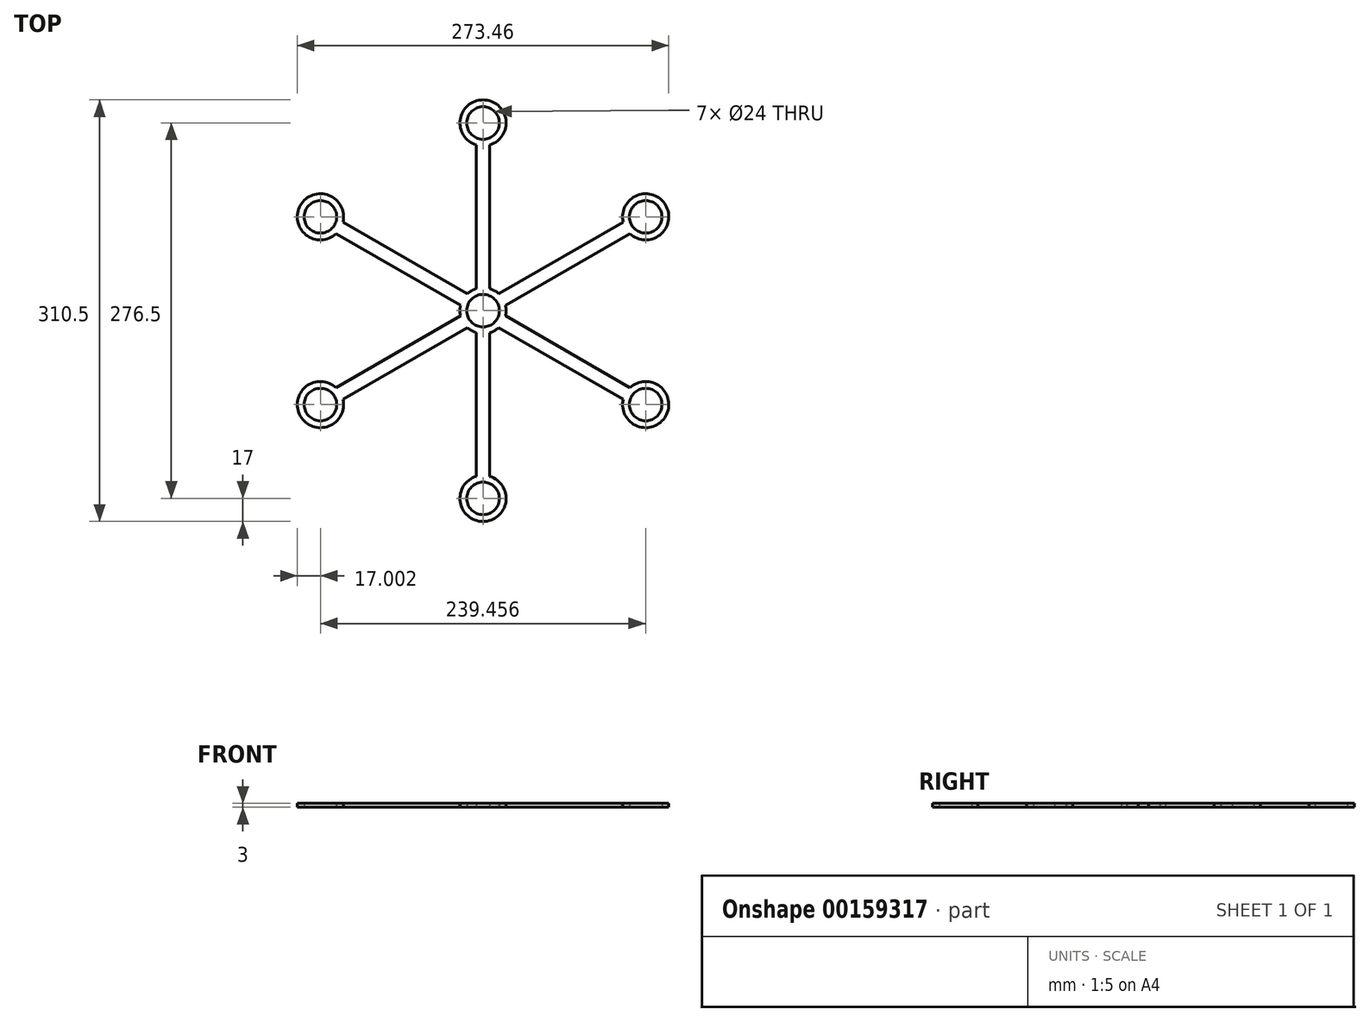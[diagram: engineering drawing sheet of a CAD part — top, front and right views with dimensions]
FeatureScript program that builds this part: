
annotation { "Feature Type Name" : "Feature", "Feature Type Description" : "" }
export const myFeature = defineFeature(function(context is Context, id is Id, definition is map)
    precondition{}
    {
        {
            var Q0;
            Q0=qCreatedBy(makeId("Top.planeOp"),FACE);
            var sketch = newSketch(context, id + "F0", { "sketchPlane" : qUnion([Q0])});
            skLineSegment(sketch, "E0", {"start": v(0, 0) * mm, "end": v(0, 138.25) * mm, "construction": true});
            skCircle(sketch, "E1", {"center": v(0, 0) * mm, "radius": 12 * mm});
            skCircle(sketch, "E2", {"center": v(0, 138.25) * mm, "radius": 12 * mm});
            skArc(sketch, "E3", {"start": v(5, 122) * mm, "mid": v(0, 155.25) * mm, "end": v(-5, 122) * mm});
            skArc(sketch, "E4", {"start": v(-16.57, 3.8) * mm, "mid": v(-17, 0) * mm, "end": v(-16.57, -3.8) * mm});
            skLineSegment(sketch, "E5", {"start": v(-5, 122) * mm, "end": v(-5, 16.25) * mm});
            skLineSegment(sketch, "E6", {"start": v(5, 122) * mm, "end": v(5, 16.25) * mm});
            skLineSegment(sketch, "E7.1.1", {"start": v(-108.16, 56.67) * mm, "end": v(-16.57, 3.8) * mm});
            skArc(sketch, "E7.1.2", {"start": v(-103.16, 65.33) * mm, "mid": v(-134.45, 77.63) * mm, "end": v(-108.16, 56.67) * mm});
            skLineSegment(sketch, "E7.1.3", {"start": v(-103.16, 65.33) * mm, "end": v(-11.57, 12.45) * mm});
            skCircle(sketch, "E7.1.4", {"center": v(-119.73, 69.13) * mm, "radius": 12 * mm});
            skLineSegment(sketch, "E7.1.6", {"start": v(0, 0) * mm, "end": v(-119.73, 69.13) * mm, "construction": true});
            skArc(sketch, "E7.2.0", {"start": v(-5, 16.25) * mm, "mid": v(-8.5, 14.72) * mm, "end": v(-11.57, 12.45) * mm});
            skLineSegment(sketch, "E7.2.1", {"start": v(-103.16, -65.33) * mm, "end": v(-11.57, -12.45) * mm});
            skArc(sketch, "E7.2.2", {"start": v(-108.16, -56.67) * mm, "mid": v(-134.45, -77.62) * mm, "end": v(-103.16, -65.33) * mm});
            skLineSegment(sketch, "E7.2.3", {"start": v(-108.16, -56.67) * mm, "end": v(-16.57, -3.8) * mm});
            skCircle(sketch, "E7.2.4", {"center": v(-119.73, -69.12) * mm, "radius": 12 * mm});
            skLineSegment(sketch, "E7.2.6", {"start": v(0, 0) * mm, "end": v(-119.73, -69.13) * mm, "construction": true});
            skArc(sketch, "E7.3.0", {"start": v(-5, 16.25) * mm, "mid": v(-8.5, 14.72) * mm, "end": v(-11.57, 12.45) * mm});
            skLineSegment(sketch, "E7.3.1", {"start": v(5, -122) * mm, "end": v(5, -16.25) * mm});
            skArc(sketch, "E7.3.2", {"start": v(-5, -122) * mm, "mid": v(0, -155.25) * mm, "end": v(5, -122) * mm});
            skLineSegment(sketch, "E7.3.3", {"start": v(-5, -122) * mm, "end": v(-5, -16.25) * mm});
            skCircle(sketch, "E7.3.4", {"center": v(0, -138.25) * mm, "radius": 12 * mm});
            skLineSegment(sketch, "E7.3.6", {"start": v(0, 0) * mm, "end": v(0, -138.25) * mm, "construction": true});
            skLineSegment(sketch, "E7.4.1", {"start": v(108.16, -56.67) * mm, "end": v(16.57, -3.8) * mm});
            skArc(sketch, "E7.4.2", {"start": v(103.16, -65.33) * mm, "mid": v(134.45, -77.63) * mm, "end": v(108.16, -56.67) * mm});
            skLineSegment(sketch, "E7.4.3", {"start": v(103.16, -65.33) * mm, "end": v(11.57, -12.45) * mm});
            skCircle(sketch, "E7.4.4", {"center": v(119.73, -69.13) * mm, "radius": 12 * mm});
            skLineSegment(sketch, "E7.4.6", {"start": v(0, 0) * mm, "end": v(119.73, -69.13) * mm, "construction": true});
            skArc(sketch, "E7.5.0", {"start": v(-5, 16.25) * mm, "mid": v(-8.5, 14.72) * mm, "end": v(-11.57, 12.45) * mm});
            skLineSegment(sketch, "E7.5.1", {"start": v(103.16, 65.33) * mm, "end": v(11.57, 12.45) * mm});
            skArc(sketch, "E7.5.2", {"start": v(108.16, 56.67) * mm, "mid": v(134.45, 77.63) * mm, "end": v(103.16, 65.33) * mm});
            skLineSegment(sketch, "E7.5.3", {"start": v(108.16, 56.67) * mm, "end": v(16.57, 3.8) * mm});
            skCircle(sketch, "E7.5.4", {"center": v(119.73, 69.13) * mm, "radius": 12 * mm});
            skLineSegment(sketch, "E7.5.6", {"start": v(0, 0) * mm, "end": v(119.73, 69.13) * mm, "construction": true});
            skArc(sketch, "E8.trimOffspring", {"start": v(11.57, 12.45) * mm, "mid": v(8.5, 14.72) * mm, "end": v(5, 16.25) * mm});
            skArc(sketch, "E9.trimOffspring", {"start": v(16.57, -3.8) * mm, "mid": v(17, 0) * mm, "end": v(16.57, 3.8) * mm});
            skArc(sketch, "E10.trimOffspring", {"start": v(5, -16.25) * mm, "mid": v(8.5, -14.72) * mm, "end": v(11.57, -12.45) * mm});
            skArc(sketch, "E11.trimOffspring", {"start": v(-11.57, -12.45) * mm, "mid": v(-8.5, -14.72) * mm, "end": v(-5, -16.25) * mm});
            skSolve(sketch);
        }
        {
            var Q0;
            Q0 = qSketchRegion(id + "F0", true);
            extrude(context, id + "F1", {"entities" : qUnion([Q0]), "depth" : 3 * mm});
        }
    });
